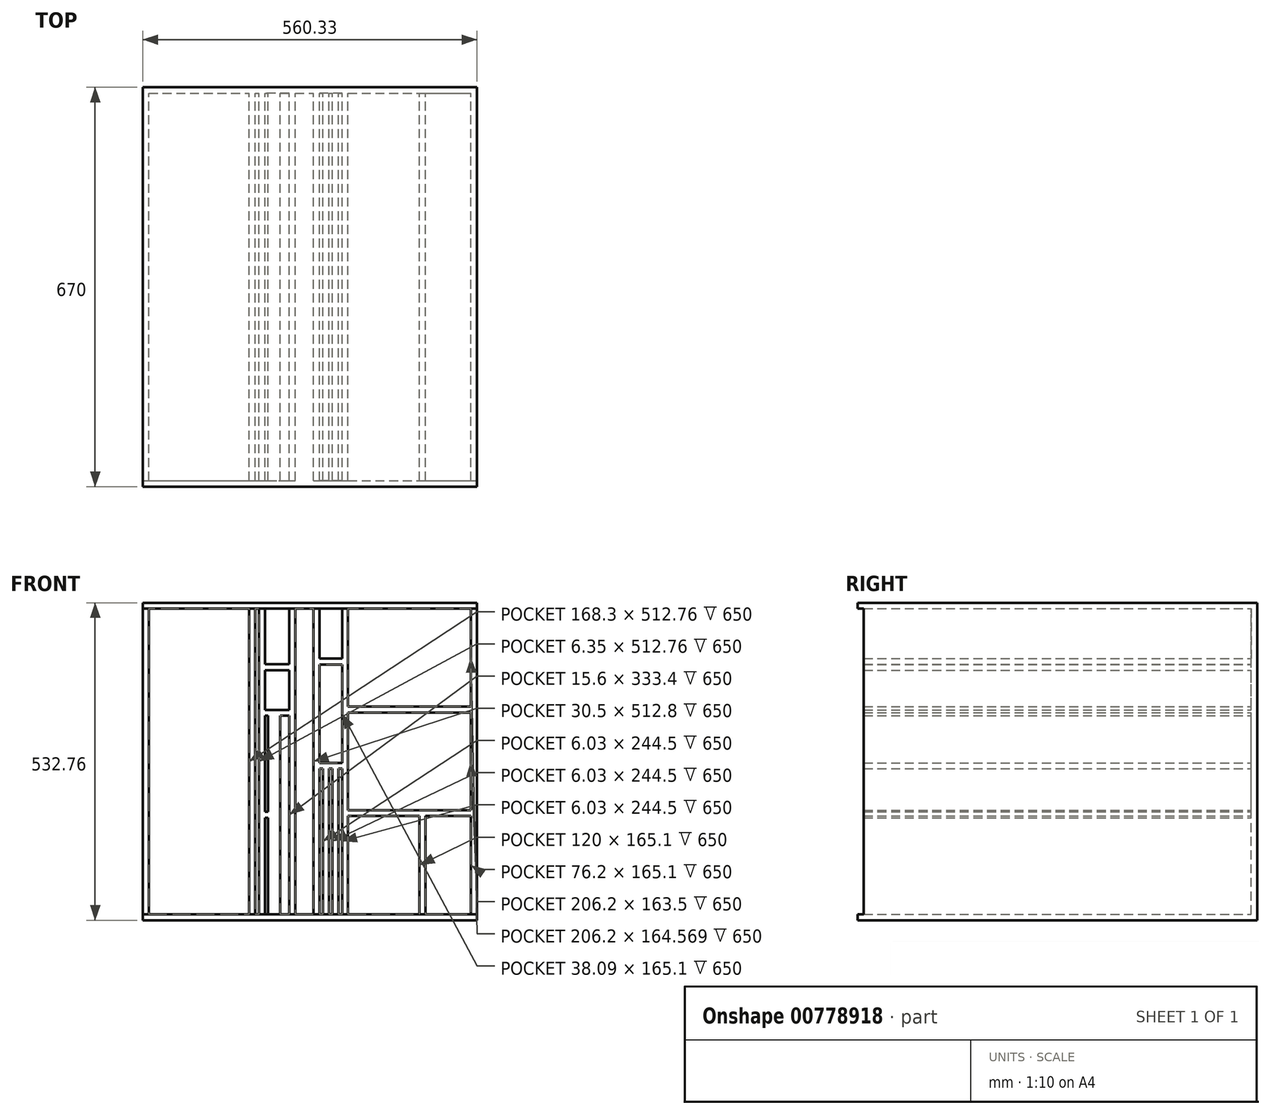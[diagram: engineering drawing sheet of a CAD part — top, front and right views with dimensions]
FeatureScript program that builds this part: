
annotation { "Feature Type Name" : "Feature", "Feature Type Description" : "" }
export const myFeature = defineFeature(function(context is Context, id is Id, definition is map)
    precondition{}
    {
        {
            var Q0;
            Q0=qCreatedBy(makeId("Front.planeOp"),FACE);
            var sketch = newSketch(context, id + "F0", { "sketchPlane" : qUnion([Q0])});
            skLineSegment(sketch, "E0.bottom", {"start": v(-281.61, 293.9) * mm, "end": v(278.72, 293.9) * mm});
            skLineSegment(sketch, "E0.top", {"start": v(-281.61, -238.85) * mm, "end": v(278.72, -238.85) * mm});
            skLineSegment(sketch, "E0.left", {"start": v(-281.61, 293.9) * mm, "end": v(-281.61, -238.85) * mm});
            skLineSegment(sketch, "E0.right", {"start": v(278.72, 293.9) * mm, "end": v(278.72, -238.85) * mm});
            skLineSegment(sketch, "E1.bottom", {"start": v(-271.61, -228.85) * mm, "end": v(-103.31, -228.85) * mm});
            skLineSegment(sketch, "E1.top", {"start": v(-271.61, 283.9) * mm, "end": v(-103.31, 283.9) * mm});
            skLineSegment(sketch, "E1.left", {"start": v(-271.61, -228.85) * mm, "end": v(-271.61, 283.9) * mm});
            skLineSegment(sketch, "E1.right", {"start": v(-103.31, -228.85) * mm, "end": v(-103.31, 283.9) * mm});
            skPoint(sketch, "E2", {"position": v(-93.31, -228.85) * mm});
            skLineSegment(sketch, "E3.bottom", {"start": v(-93.31, -228.85) * mm, "end": v(-86.96, -228.85) * mm});
            skLineSegment(sketch, "E3.top", {"start": v(-93.31, 283.9) * mm, "end": v(-86.96, 283.9) * mm});
            skLineSegment(sketch, "E3.left", {"start": v(-93.31, -228.85) * mm, "end": v(-93.31, 283.9) * mm});
            skLineSegment(sketch, "E3.right", {"start": v(-86.96, -228.85) * mm, "end": v(-86.96, 283.9) * mm});
            skPoint(sketch, "E4", {"position": v(-76.96, -228.85) * mm});
            skLineSegment(sketch, "E5.bottom", {"start": v(-76.96, -228.85) * mm, "end": v(-71.88, -228.85) * mm});
            skLineSegment(sketch, "E5.top", {"start": v(-76.96, -67.15) * mm, "end": v(-71.88, -67.15) * mm});
            skLineSegment(sketch, "E5.left", {"start": v(-76.96, -228.85) * mm, "end": v(-76.96, -67.15) * mm});
            skLineSegment(sketch, "E5.right", {"start": v(-71.88, -228.85) * mm, "end": v(-71.88, -67.15) * mm});
            skLineSegment(sketch, "E6.bottom", {"start": v(-76.96, -57.15) * mm, "end": v(-71.88, -57.15) * mm});
            skLineSegment(sketch, "E6.top", {"start": v(-76.96, 104.55) * mm, "end": v(-71.88, 104.55) * mm});
            skLineSegment(sketch, "E6.left", {"start": v(-76.96, -57.15) * mm, "end": v(-76.96, 104.55) * mm});
            skLineSegment(sketch, "E6.right", {"start": v(-71.88, -57.15) * mm, "end": v(-71.88, 104.55) * mm});
            skPoint(sketch, "E7", {"position": v(-51.67, -228.85) * mm});
            skLineSegment(sketch, "E8.bottom", {"start": v(-51.67, -228.85) * mm, "end": v(-36.07, -228.85) * mm});
            skLineSegment(sketch, "E8.top", {"start": v(-51.67, 104.55) * mm, "end": v(-36.07, 104.55) * mm});
            skLineSegment(sketch, "E8.left", {"start": v(-51.67, -228.85) * mm, "end": v(-51.67, 104.55) * mm});
            skLineSegment(sketch, "E8.right", {"start": v(-36.07, -228.85) * mm, "end": v(-36.07, 104.55) * mm});
            skLineSegment(sketch, "E9.bottom", {"start": v(-36.07, 113.9) * mm, "end": v(-76.96, 113.9) * mm});
            skLineSegment(sketch, "E9.top", {"start": v(-36.07, 180.6) * mm, "end": v(-76.96, 180.6) * mm});
            skLineSegment(sketch, "E9.left", {"start": v(-36.07, 113.9) * mm, "end": v(-36.07, 180.6) * mm});
            skLineSegment(sketch, "E9.right", {"start": v(-76.96, 113.9) * mm, "end": v(-76.96, 180.6) * mm});
            skLineSegment(sketch, "E10.bottom", {"start": v(-26.07, -228.85) * mm, "end": v(4.43, -228.85) * mm});
            skLineSegment(sketch, "E10.top", {"start": v(-26.07, 283.95) * mm, "end": v(4.43, 283.95) * mm});
            skLineSegment(sketch, "E10.left", {"start": v(-26.07, -228.85) * mm, "end": v(-26.07, 283.95) * mm});
            skLineSegment(sketch, "E10.right", {"start": v(4.43, -228.85) * mm, "end": v(4.43, 283.95) * mm});
            skLineSegment(sketch, "E11.bottom", {"start": v(14.43, -228.85) * mm, "end": v(20.46, -228.85) * mm});
            skLineSegment(sketch, "E11.top", {"start": v(14.43, 15.65) * mm, "end": v(20.46, 15.65) * mm});
            skLineSegment(sketch, "E11.left", {"start": v(14.43, -228.85) * mm, "end": v(14.43, 15.65) * mm});
            skLineSegment(sketch, "E11.right", {"start": v(20.46, -228.85) * mm, "end": v(20.46, 15.65) * mm});
            skLineSegment(sketch, "E12.bottom", {"start": v(30.46, -228.85) * mm, "end": v(36.49, -228.85) * mm});
            skLineSegment(sketch, "E12.top", {"start": v(30.46, 15.65) * mm, "end": v(36.49, 15.65) * mm});
            skLineSegment(sketch, "E12.left", {"start": v(30.46, -228.85) * mm, "end": v(30.46, 15.65) * mm});
            skLineSegment(sketch, "E12.right", {"start": v(36.49, -228.85) * mm, "end": v(36.49, 15.65) * mm});
            skLineSegment(sketch, "E13.bottom", {"start": v(46.49, -228.85) * mm, "end": v(52.52, -228.85) * mm});
            skLineSegment(sketch, "E13.top", {"start": v(46.49, 15.65) * mm, "end": v(52.52, 15.65) * mm});
            skLineSegment(sketch, "E13.left", {"start": v(46.49, -228.85) * mm, "end": v(46.49, 15.65) * mm});
            skLineSegment(sketch, "E13.right", {"start": v(52.52, -228.85) * mm, "end": v(52.52, 15.65) * mm});
            skLineSegment(sketch, "E14.bottom", {"start": v(52.52, 24.96) * mm, "end": v(14.43, 24.96) * mm});
            skLineSegment(sketch, "E14.top", {"start": v(52.52, 190.06) * mm, "end": v(14.43, 190.06) * mm});
            skLineSegment(sketch, "E14.left", {"start": v(52.52, 24.96) * mm, "end": v(52.52, 190.06) * mm});
            skLineSegment(sketch, "E14.right", {"start": v(14.43, 24.96) * mm, "end": v(14.43, 190.06) * mm});
            skLineSegment(sketch, "E15.bottom", {"start": v(62.52, -228.85) * mm, "end": v(182.52, -228.85) * mm});
            skLineSegment(sketch, "E15.top", {"start": v(62.52, -63.75) * mm, "end": v(182.52, -63.75) * mm});
            skLineSegment(sketch, "E15.left", {"start": v(62.52, -228.85) * mm, "end": v(62.52, -63.75) * mm});
            skLineSegment(sketch, "E15.right", {"start": v(182.52, -228.85) * mm, "end": v(182.52, -63.75) * mm});
            skLineSegment(sketch, "E16.bottom", {"start": v(192.52, -228.85) * mm, "end": v(268.72, -228.85) * mm});
            skLineSegment(sketch, "E16.top", {"start": v(192.52, -63.75) * mm, "end": v(268.72, -63.75) * mm});
            skLineSegment(sketch, "E16.left", {"start": v(192.52, -228.85) * mm, "end": v(192.52, -63.75) * mm});
            skLineSegment(sketch, "E16.right", {"start": v(268.72, -228.85) * mm, "end": v(268.72, -63.75) * mm});
            skLineSegment(sketch, "E17.bottom", {"start": v(62.52, -54.12) * mm, "end": v(268.72, -54.12) * mm});
            skLineSegment(sketch, "E17.top", {"start": v(62.52, 109.38) * mm, "end": v(268.72, 109.38) * mm});
            skLineSegment(sketch, "E17.left", {"start": v(62.52, -54.12) * mm, "end": v(62.52, 109.38) * mm});
            skLineSegment(sketch, "E17.right", {"start": v(268.72, -54.12) * mm, "end": v(268.72, 109.38) * mm});
            skLineSegment(sketch, "E18.bottom", {"start": v(-76.96, 190.6) * mm, "end": v(-36.07, 190.6) * mm});
            skLineSegment(sketch, "E18.top", {"start": v(-76.96, 283.9) * mm, "end": v(-36.07, 283.9) * mm});
            skLineSegment(sketch, "E18.left", {"start": v(-76.96, 190.6) * mm, "end": v(-76.96, 283.9) * mm});
            skLineSegment(sketch, "E18.right", {"start": v(-36.07, 190.6) * mm, "end": v(-36.07, 283.9) * mm});
            skLineSegment(sketch, "E19.bottom", {"start": v(14.43, 283.95) * mm, "end": v(52.52, 283.95) * mm});
            skLineSegment(sketch, "E19.top", {"start": v(14.43, 200.06) * mm, "end": v(52.52, 200.06) * mm});
            skLineSegment(sketch, "E19.left", {"start": v(14.43, 283.95) * mm, "end": v(14.43, 200.06) * mm});
            skLineSegment(sketch, "E19.right", {"start": v(52.52, 283.95) * mm, "end": v(52.52, 200.06) * mm});
            skLineSegment(sketch, "E20.bottom", {"start": v(62.52, 119.38) * mm, "end": v(268.72, 119.38) * mm});
            skLineSegment(sketch, "E20.top", {"start": v(62.52, 283.95) * mm, "end": v(268.72, 283.95) * mm});
            skLineSegment(sketch, "E20.left", {"start": v(62.52, 119.38) * mm, "end": v(62.52, 283.95) * mm});
            skLineSegment(sketch, "E20.right", {"start": v(268.72, 119.38) * mm, "end": v(268.72, 283.95) * mm});
            skSolve(sketch);
        }
        {
            var Q0;
            Q0 = qSketchRegion(id + "F0", true);
            extrude(context, id + "F1", {"entities" : qUnion([Q0]), "depth" : 650 * mm, "offsetDistance" : 25.4 * mm});
        }
        {
            var Q0;
            Q0=makeQuery(id+"F1.opExtrude","SWEPT_FACE",FACE,{"disambiguationData":[OSD([sQuery(id+"F0.wireOp",EDGE,"E0.left")])]});
            var sketch = newSketch(context, id + "F2", { "sketchPlane" : qUnion([Q0])});
            skLineSegment(sketch, "E21.bottom", {"start": v(0, 293.9) * mm, "end": v(-10, 293.9) * mm});
            skLineSegment(sketch, "E21.top", {"start": v(0, -238.85) * mm, "end": v(-10, -238.85) * mm});
            skLineSegment(sketch, "E21.left", {"start": v(0, 293.9) * mm, "end": v(0, -238.85) * mm});
            skLineSegment(sketch, "E21.right", {"start": v(-10, 293.9) * mm, "end": v(-10, -238.85) * mm});
            skSolve(sketch);
        }
        {
            var Q0;
            Q0 = qSketchRegion(id + "F2", true);
            var Q1;
            Q1=makeQuery(id+"F1.opExtrude","SWEPT_FACE",FACE,{"disambiguationData":[OSD([sQuery(id+"F0.wireOp",EDGE,"E0.right")])]});
            extrude(context, id + "F3", {"entities" : qUnion([Q0]), "operationType" : NewBodyOperationType.ADD, "endBound" : BoundingType.UP_TO_SURFACE, "oppositeDirection" : true, "depth" : 25.4 * mm, "endBoundEntityFace" : qUnion([Q1]), "offsetDistance" : 25.4 * mm});
        }
        {
            var Q0;
            Q0=makeQuery(id+"F1.opExtrude","CAP_FACE",FACE,{"disambiguationData":[OSD([sQuery(id+"F0.wireOp",EDGE,"E0.bottom"),sQuery(id+"F0.wireOp",EDGE,"E0.top"),sQuery(id+"F0.wireOp",EDGE,"E0.left"),sQuery(id+"F0.wireOp",EDGE,"E0.right"),sQuery(id+"F0.wireOp",EDGE,"E1.bottom"),sQuery(id+"F0.wireOp",EDGE,"E1.top"),sQuery(id+"F0.wireOp",EDGE,"E1.left"),sQuery(id+"F0.wireOp",EDGE,"E1.right"),sQuery(id+"F0.wireOp",EDGE,"E3.bottom"),sQuery(id+"F0.wireOp",EDGE,"E3.top"),sQuery(id+"F0.wireOp",EDGE,"E3.left"),sQuery(id+"F0.wireOp",EDGE,"E3.right"),sQuery(id+"F0.wireOp",EDGE,"E5.bottom"),sQuery(id+"F0.wireOp",EDGE,"E5.top"),sQuery(id+"F0.wireOp",EDGE,"E5.left"),sQuery(id+"F0.wireOp",EDGE,"E5.right"),sQuery(id+"F0.wireOp",EDGE,"E6.bottom"),sQuery(id+"F0.wireOp",EDGE,"E6.top"),sQuery(id+"F0.wireOp",EDGE,"E6.left"),sQuery(id+"F0.wireOp",EDGE,"E6.right"),sQuery(id+"F0.wireOp",EDGE,"E8.bottom"),sQuery(id+"F0.wireOp",EDGE,"E8.top"),sQuery(id+"F0.wireOp",EDGE,"E8.left"),sQuery(id+"F0.wireOp",EDGE,"E8.right"),sQuery(id+"F0.wireOp",EDGE,"E9.bottom"),sQuery(id+"F0.wireOp",EDGE,"E9.top"),sQuery(id+"F0.wireOp",EDGE,"E9.left"),sQuery(id+"F0.wireOp",EDGE,"E9.right"),sQuery(id+"F0.wireOp",EDGE,"E10.bottom"),sQuery(id+"F0.wireOp",EDGE,"E10.top"),sQuery(id+"F0.wireOp",EDGE,"E10.left"),sQuery(id+"F0.wireOp",EDGE,"E10.right"),sQuery(id+"F0.wireOp",EDGE,"E11.bottom"),sQuery(id+"F0.wireOp",EDGE,"E11.top"),sQuery(id+"F0.wireOp",EDGE,"E11.left"),sQuery(id+"F0.wireOp",EDGE,"E11.right"),sQuery(id+"F0.wireOp",EDGE,"E12.bottom"),sQuery(id+"F0.wireOp",EDGE,"E12.top"),sQuery(id+"F0.wireOp",EDGE,"E12.left"),sQuery(id+"F0.wireOp",EDGE,"E12.right"),sQuery(id+"F0.wireOp",EDGE,"E13.bottom"),sQuery(id+"F0.wireOp",EDGE,"E13.top"),sQuery(id+"F0.wireOp",EDGE,"E13.left"),sQuery(id+"F0.wireOp",EDGE,"E13.right"),sQuery(id+"F0.wireOp",EDGE,"E14.bottom"),sQuery(id+"F0.wireOp",EDGE,"E14.top"),sQuery(id+"F0.wireOp",EDGE,"E14.left"),sQuery(id+"F0.wireOp",EDGE,"E14.right"),sQuery(id+"F0.wireOp",EDGE,"E15.bottom"),sQuery(id+"F0.wireOp",EDGE,"E15.top"),sQuery(id+"F0.wireOp",EDGE,"E15.left"),sQuery(id+"F0.wireOp",EDGE,"E15.right"),sQuery(id+"F0.wireOp",EDGE,"E16.bottom"),sQuery(id+"F0.wireOp",EDGE,"E16.top"),sQuery(id+"F0.wireOp",EDGE,"E16.left"),sQuery(id+"F0.wireOp",EDGE,"E16.right"),sQuery(id+"F0.wireOp",EDGE,"E17.bottom"),sQuery(id+"F0.wireOp",EDGE,"E17.top"),sQuery(id+"F0.wireOp",EDGE,"E17.left"),sQuery(id+"F0.wireOp",EDGE,"E17.right"),sQuery(id+"F0.wireOp",EDGE,"E18.bottom"),sQuery(id+"F0.wireOp",EDGE,"E18.top"),sQuery(id+"F0.wireOp",EDGE,"E18.left"),sQuery(id+"F0.wireOp",EDGE,"E18.right"),sQuery(id+"F0.wireOp",EDGE,"E19.bottom"),sQuery(id+"F0.wireOp",EDGE,"E19.top"),sQuery(id+"F0.wireOp",EDGE,"E19.left"),sQuery(id+"F0.wireOp",EDGE,"E19.right"),sQuery(id+"F0.wireOp",EDGE,"E20.bottom"),sQuery(id+"F0.wireOp",EDGE,"E20.top"),sQuery(id+"F0.wireOp",EDGE,"E20.left"),sQuery(id+"F0.wireOp",EDGE,"E20.right")])],"isStart":false});
            var sketch = newSketch(context, id + "F4", { "sketchPlane" : qUnion([Q0])});
            skLineSegment(sketch, "E22.bottom", {"start": v(-281.61, 293.9) * mm, "end": v(278.72, 293.9) * mm});
            skLineSegment(sketch, "E22.top", {"start": v(-281.61, 283.95) * mm, "end": v(278.72, 283.95) * mm});
            skLineSegment(sketch, "E22.left", {"start": v(-281.61, 293.9) * mm, "end": v(-281.61, 283.95) * mm});
            skLineSegment(sketch, "E22.right", {"start": v(278.72, 293.9) * mm, "end": v(278.72, 283.95) * mm});
            skLineSegment(sketch, "E23.bottom", {"start": v(-281.61, -238.85) * mm, "end": v(278.72, -238.85) * mm});
            skLineSegment(sketch, "E23.top", {"start": v(-281.61, -228.85) * mm, "end": v(278.72, -228.85) * mm});
            skLineSegment(sketch, "E23.left", {"start": v(-281.61, -238.85) * mm, "end": v(-281.61, -228.85) * mm});
            skLineSegment(sketch, "E23.right", {"start": v(278.72, -238.85) * mm, "end": v(278.72, -228.85) * mm});
            skSolve(sketch);
        }
        {
            var Q0;
            Q0 = qSketchRegion(id + "F4", true);
            extrude(context, id + "F5", {"entities" : qUnion([Q0]), "operationType" : NewBodyOperationType.ADD, "depth" : 10 * mm, "offsetDistance" : 25.4 * mm});
        }
    });
